# Revit family: 111213014025804
name_source: partatom
category: Modelos genéricos
revit_build: Autodesk Revit 2018 (Build: 20190510_1515(x64)
units: mm (PartAtom-declared; Revit-internal decimal feet)

## family parameters
Compartido = No
Corte con vacíos al cargar = No
Cota de conector redondo = Diámetro de uso
Puede alojar armadura = No
Punto de cálculo de habitación = No
Se basa en plano de trabajo = No
Siempre vertical = No
Tipo de pieza = Normal

## types (1)
- GRADA ESTOPEROL GOMA 320X4MM NEGRO 1.50
    Alto = 50 mm  [stored 0.164042 ft]
    Aplicacion = Escaleras
    Color = Negro - Gris (Consultar por Beige y Café)
    Descripción = Grada Estoperol Goma 320x4MM.
    Dimension = 300 mm
    Empresa = CNP SPA.
    Espesor = 4 mm  [stored 0.0131234 ft]
    Largo = 1500 mm  [stored 4.92126 ft]
    Material = Goma negro
    Modelo = GRADA ESTOPEROL GOMA 320X4MM
    Nombre SKU = GRADA ESTOPEROL GOMA 320X4MM NEGRO TIRA 1.5MT
    Num SKUs = 111213014025804
    URL = https://www.empresascnp.cl
    Unidad = Tiras de 1.20 Mts y 1.50 Mts.
    Url Ficha tecnica = https://empresascnp.cl
    Uso = Grada de Goma son fabricadas en caucho natural, ideal para zonas de alto tráfico,
modelo estoperol. Ideal para: Edificios Públicos y Privados, Colegios, Universidades,
Centros comerciales, Aeropuertos, Hoteles, Edificios Habitacionales, entre otros.

note: [stored X ft] marks values corroborated as IEEE doubles in the binary element streams (Revit-internal decimal feet)
